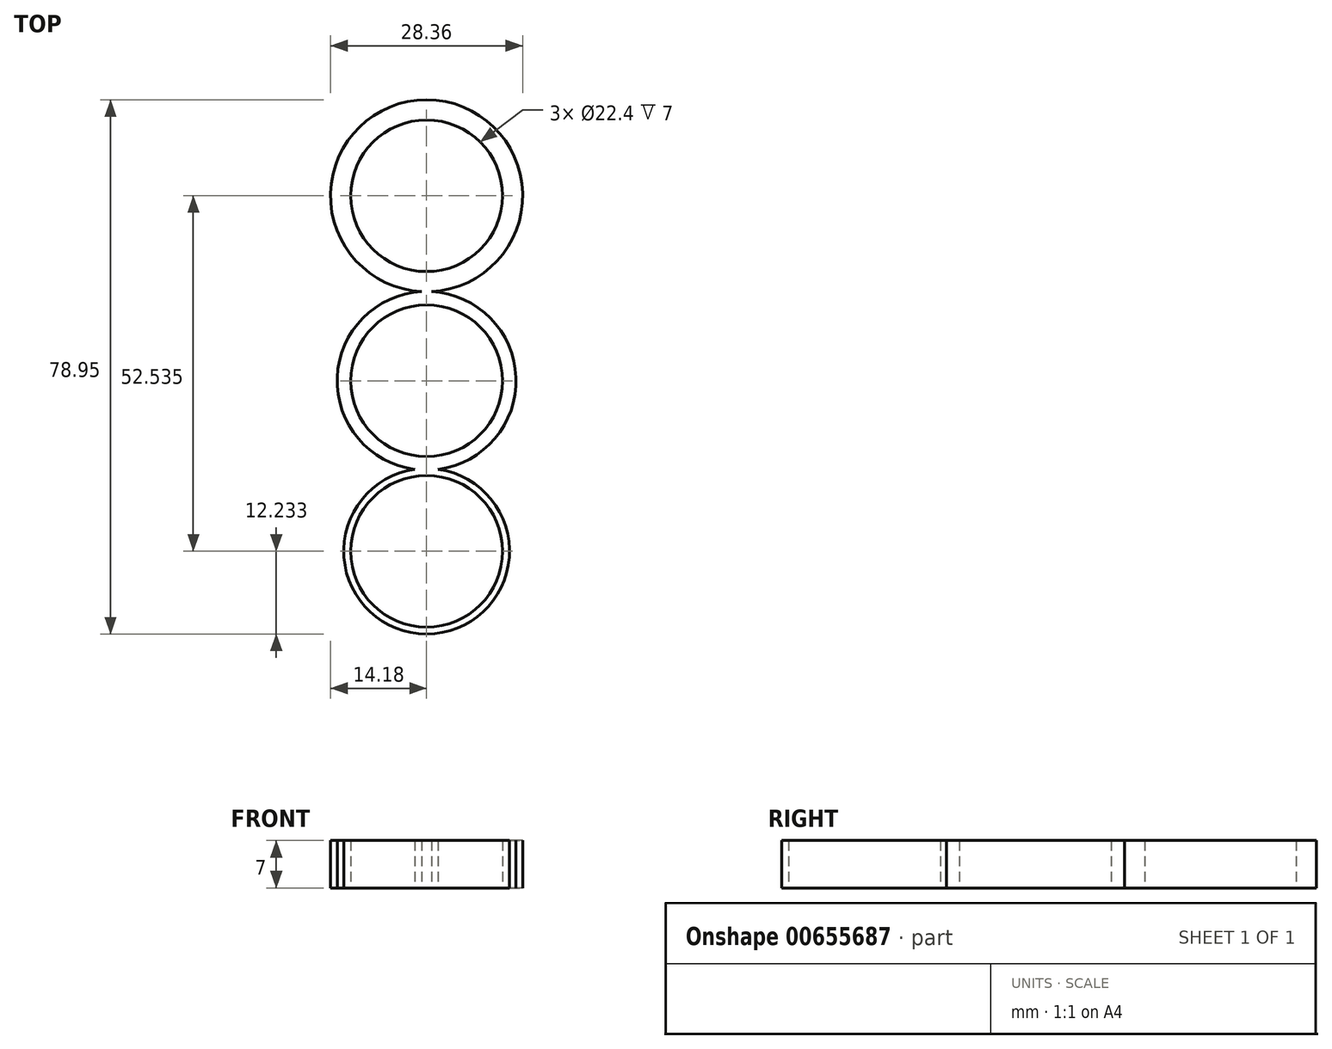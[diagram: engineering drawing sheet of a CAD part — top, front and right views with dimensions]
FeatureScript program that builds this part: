
annotation { "Feature Type Name" : "Feature", "Feature Type Description" : "" }
export const myFeature = defineFeature(function(context is Context, id is Id, definition is map)
    precondition{}
    {
        {
            var Q0;
            Q0=qCreatedBy(makeId("Top.planeOp"),FACE);
            var sketch = newSketch(context, id + "F0", { "sketchPlane" : qUnion([Q0])});
            skCircle(sketch, "E0", {"center": v(0, 0) * mm, "radius": 11.2 * mm});
            skCircle(sketch, "E1", {"center": v(0, 0) * mm, "radius": 13.2 * mm});
            skCircle(sketch, "E2", {"center": v(0, 27.34) * mm, "radius": 11.2 * mm});
            skCircle(sketch, "E3", {"center": v(0, 27.34) * mm, "radius": 14.18 * mm});
            skCircle(sketch, "E4", {"center": v(0, -25.2) * mm, "radius": 11.2 * mm});
            skCircle(sketch, "E5", {"center": v(0, -25.2) * mm, "radius": 12.23 * mm});
            skSolve(sketch);
        }
        {
            var Q0;
            Q0 = qSketchRegion(id + "F0", true);
            extrude(context, id + "F1", {"entities" : qUnion([Q0]), "depth" : 7 * mm, "offsetDistance" : 25 * mm});
        }
    });
